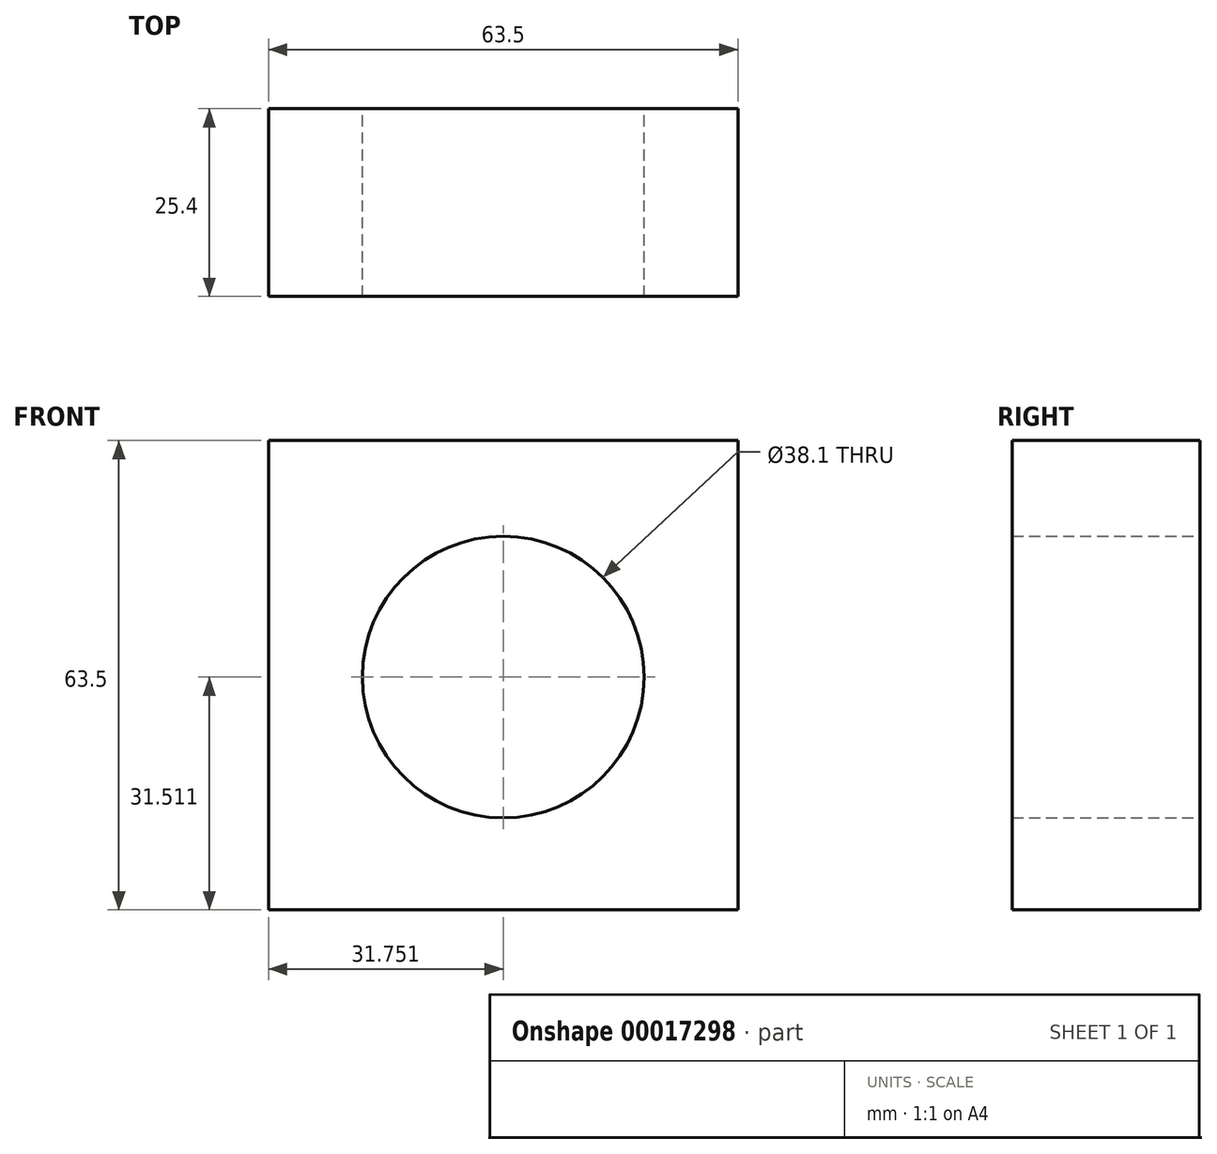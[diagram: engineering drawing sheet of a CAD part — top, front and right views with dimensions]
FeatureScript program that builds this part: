
annotation { "Feature Type Name" : "Feature", "Feature Type Description" : "" }
export const myFeature = defineFeature(function(context is Context, id is Id, definition is map)
    precondition{}
    {
        {
            var Q0;
            Q0=qCreatedBy(makeId("Front.planeOp"),FACE);
            var sketch = newSketch(context, id + "F0", { "sketchPlane" : qUnion([Q0])});
            skLineSegment(sketch, "E0", {"start": v(-21.34, 32.23) * mm, "end": v(-21.34, -31.27) * mm});
            skLineSegment(sketch, "E1", {"start": v(-21.34, -31.27) * mm, "end": v(42.16, -31.27) * mm});
            skLineSegment(sketch, "E2", {"start": v(42.16, -31.27) * mm, "end": v(42.16, 32.23) * mm});
            skLineSegment(sketch, "E3", {"start": v(42.16, 32.23) * mm, "end": v(-21.34, 32.23) * mm});
            skCircle(sketch, "E4", {"center": v(10.41, 0.24) * mm, "radius": 19.05 * mm});
            skSolve(sketch);
        }
        {
            var Q0;
            Q0 = qSketchRegion(id + "F0", true);
            extrude(context, id + "F1", {"entities" : qUnion([Q0]), "depth" : 25.4 * mm});
        }
    });
